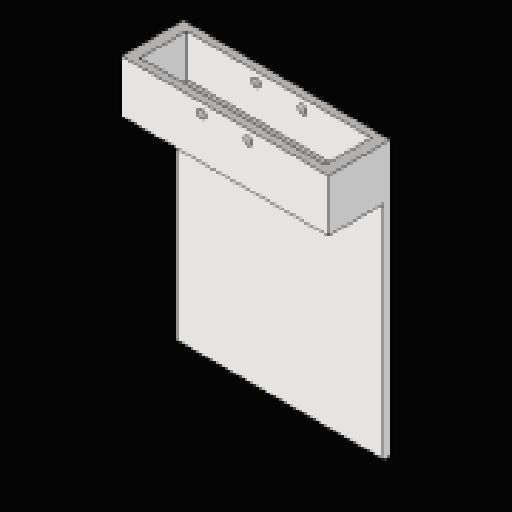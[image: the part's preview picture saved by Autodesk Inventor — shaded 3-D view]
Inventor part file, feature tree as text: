
AUTODESK INVENTOR PART (.ipt)
format: ipt  version: 2023.2 (Build 272271030, 271C)  size: 183,808 bytes
history: native  units: mm
features: sketch x5, extrude x4, projected_geometry x4, reference x4, other x4, hole x1
ambient origin geometry x8: Origin, YZ Plane, XZ Plane, XY Plane, X Axis, Y Axis, Z Axis, Center Point
bodies: Solid1 (feature_tree)
feature tree (22):
  extrude  "Extrusion1"  Depth=100.0mm
  extrude  "Extrusion2"  Depth=3.0mm
  extrude  "Extrusion3"  Depth=7.65mm
  hole  "Hole1"  [1 undecoded]
  extrude  "Extrusion4"  Depth=12.7mm
  sketch  "Sketch1"  dims[d0=93.4mm d1=100.0mm]
  sketch  "Sketch2"  dims[d2=3.0mm d3=0.0mm d4=3.0mm]
  projected_geometry  "Projected Loop1"
  reference  "Reference1"
  reference  "Reference2"
  reference  "Reference3"
  reference  "Reference4"
  sketch  "Sketch3"  dims[d6=9.8mm d7=7.65mm]
  projected_geometry  "Projected Loop2"
  sketch  "Sketch4"  dims[d8=23.0mm d9=9.8mm]
  projected_geometry  "Projected Loop3"
  sketch  "Sketch5"  dims[d11=4.5mm d12=0.0mm d13=12.7mm d14=28.0mm d15=7.65mm d16=2.5mm d17=5.0mm d18=5.0mm d19=22.0mm d20=19.0mm d21=0.0mm d23=36.2mm d24=36.2mm d25=4.55mm d26=4.0mm d27=6.0mm d28=8.0mm d29=8.0mm d30=90.0deg d31=8.0mm d32=20.594885mm d33=9.0mm d34=14.0mm d35=30.0mm d36=0.0mm d37=0.0mm]
  projected_geometry  "Projected Loop4"
  other  "<userpath>\OneDrive\Documents\Arduino\Onslaught\CAD\Frame Test\Frame Test.iam"
  other  "Frame Test.iam"
  other  "SG90 - Micro Servo 9g - Tower Pro:2"
  other  "SG90 - Micro Servo 9g - Tower Pro:1"
note: 1 required parameter value undecoded (feature->parameter linkage not recoverable at this tier; creation-order binding heuristic only, values carry confidence <= 0.55)
